FCSTD DOCUMENT  (FreeCAD 1.0R39319 (Git))
Label: plug-mount
License: All rights reserved
LicenseURL: https://en.wikipedia.org/wiki/All_rights_reserved
objects: Sketcher::SketchObject×2, PartDesign::Body×2
note: 6 computed .brp shape members not serialized (recipe doc carries the construction recipe); baked Part::Feature solids carry a one-line shape summary decoded from their .brp

FEATURE [Sketcher::SketchObject] Sketch  label="acrylic"
  ArcFitTolerance = 1e-06
  AttachmentSupport = -> [XY_Plane]
  FullyConstrained = true
  MakeInternals = false
  MapMode = 5
  sketch-geometry (84):
    g0: LineSegment StartX=0 StartY=9.525 StartZ=0 EndX=0 EndY=-9.525 EndZ=0
    g1: LineSegment StartX=0 StartY=-9.525 StartZ=0 EndX=12 EndY=-9.525 EndZ=0
    g2: LineSegment StartX=12 StartY=9.525 StartZ=0 EndX=0 EndY=9.525 EndZ=0
    g3: Circle CenterX=6 CenterY=12.7 CenterZ=0 NormalX=0 NormalY=0 NormalZ=1 AngleXU=0 Radius=1.5
    g4: Circle CenterX=6 CenterY=-12.7 CenterZ=0 NormalX=0 NormalY=0 NormalZ=1 AngleXU=0 Radius=1.5
    g5: LineSegment [constr] StartX=6 StartY=12.7 StartZ=0 EndX=6 EndY=-12.7 EndZ=0
    g6: LineSegment StartX=12 StartY=9.525 StartZ=0 EndX=12 EndY=-9.525 EndZ=0
    g7: GeomPoint X=6 Y=0 Z=0
    g8: LineSegment [constr] StartX=-2 StartY=17.5 StartZ=0 EndX=-2 EndY=-17.5 EndZ=0
    g9: LineSegment [constr] StartX=-2 StartY=-17.5 StartZ=0 EndX=14 EndY=-17.5 EndZ=0
    g10: LineSegment [constr] StartX=14 StartY=-17.5 StartZ=0 EndX=14 EndY=17.5 EndZ=0
    g11: LineSegment [constr] StartX=14 StartY=17.5 StartZ=0 EndX=-2 EndY=17.5 EndZ=0
    g12: LineSegment StartX=16 StartY=9.525 StartZ=0 EndX=16 EndY=-9.525 EndZ=0
    g13: LineSegment StartX=16 StartY=-9.525 StartZ=0 EndX=28 EndY=-9.525 EndZ=0
    g14: LineSegment StartX=28 StartY=9.525 StartZ=0 EndX=16 EndY=9.525 EndZ=0
    g15: Circle CenterX=22 CenterY=12.7 CenterZ=0 NormalX=0 NormalY=0 NormalZ=1 AngleXU=0 Radius=1.5
    g16: Circle CenterX=22 CenterY=-12.7 CenterZ=0 NormalX=0 NormalY=0 NormalZ=1 AngleXU=0 Radius=1.5
    g17: LineSegment [constr] StartX=22 StartY=12.7 StartZ=0 EndX=22 EndY=-12.7 EndZ=0
    g18: LineSegment StartX=28 StartY=9.525 StartZ=0 EndX=28 EndY=-9.525 EndZ=0
    g19: GeomPoint X=22 Y=5e-16 Z=0
    g20: LineSegment [constr] StartX=14 StartY=17.5 StartZ=0 EndX=14 EndY=-17.5 EndZ=0
    g21: LineSegment [constr] StartX=14 StartY=-17.5 StartZ=0 EndX=30 EndY=-17.5 EndZ=0
    g22: LineSegment [constr] StartX=30 StartY=-17.5 StartZ=0 EndX=30 EndY=17.5 EndZ=0
    g23: LineSegment [constr] StartX=30 StartY=17.5 StartZ=0 EndX=14 EndY=17.5 EndZ=0
    g24: LineSegment StartX=32 StartY=9.525 StartZ=0 EndX=32 EndY=-9.525 EndZ=0
    g25: LineSegment StartX=32 StartY=-9.525 StartZ=0 EndX=44 EndY=-9.525 EndZ=0
    g26: LineSegment StartX=44 StartY=9.525 StartZ=0 EndX=32 EndY=9.525 EndZ=0
    g27: Circle CenterX=38 CenterY=12.7 CenterZ=0 NormalX=0 NormalY=0 NormalZ=1 AngleXU=0 Radius=1.5
    g28: Circle CenterX=38 CenterY=-12.7 CenterZ=0 NormalX=0 NormalY=0 NormalZ=1 AngleXU=0 Radius=1.5
    g29: LineSegment [constr] StartX=38 StartY=12.7 StartZ=0 EndX=38 EndY=-12.7 EndZ=0
    g30: LineSegment StartX=44 StartY=9.525 StartZ=0 EndX=44 EndY=-9.525 EndZ=0
    g31: GeomPoint X=38 Y=-7e-16 Z=0
    g32: LineSegment [constr] StartX=30 StartY=17.5 StartZ=0 EndX=30 EndY=-17.5 EndZ=0
    g33: LineSegment [constr] StartX=30 StartY=-17.5 StartZ=0 EndX=46 EndY=-17.5 EndZ=0
    g34: LineSegment [constr] StartX=46 StartY=-17.5 StartZ=0 EndX=46 EndY=17.5 EndZ=0
    g35: LineSegment [constr] StartX=46 StartY=17.5 StartZ=0 EndX=30 EndY=17.5 EndZ=0
    g36: LineSegment StartX=48 StartY=9.525 StartZ=0 EndX=48 EndY=-9.525 EndZ=0
    g37: LineSegment StartX=48 StartY=-9.525 StartZ=0 EndX=60 EndY=-9.525 EndZ=0
    g38: LineSegment StartX=60 StartY=9.525 StartZ=0 EndX=48 EndY=9.525 EndZ=0
    g39: Circle CenterX=54 CenterY=12.7 CenterZ=0 NormalX=0 NormalY=0 NormalZ=1 AngleXU=0 Radius=1.5
    g40: Circle CenterX=54 CenterY=-12.7 CenterZ=0 NormalX=0 NormalY=0 NormalZ=1 AngleXU=0 Radius=1.5
    g41: LineSegment [constr] StartX=54 StartY=12.7 StartZ=0 EndX=54 EndY=-12.7 EndZ=0
    g42: LineSegment StartX=60 StartY=9.525 StartZ=0 EndX=60 EndY=-9.525 EndZ=0
    g43: GeomPoint X=54 Y=-6e-16 Z=0
    g44: LineSegment [constr] StartX=46 StartY=17.5 StartZ=0 EndX=46 EndY=-17.5 EndZ=0
    g45: LineSegment [constr] StartX=46 StartY=-17.5 StartZ=0 EndX=62 EndY=-17.5 EndZ=0
    g46: LineSegment [constr] StartX=62 StartY=-17.5 StartZ=0 EndX=62 EndY=17.5 EndZ=0
    g47: LineSegment [constr] StartX=62 StartY=17.5 StartZ=0 EndX=46 EndY=17.5 EndZ=0
    g48: LineSegment StartX=64 StartY=9.525 StartZ=0 EndX=64 EndY=-9.525 EndZ=0
    g49: LineSegment StartX=64 StartY=-9.525 StartZ=0 EndX=76 EndY=-9.525 EndZ=0
    g50: LineSegment StartX=76 StartY=9.525 StartZ=0 EndX=64 EndY=9.525 EndZ=0
    g51: Circle CenterX=70 CenterY=12.7 CenterZ=0 NormalX=0 NormalY=0 NormalZ=1 AngleXU=0 Radius=1.5
    g52: Circle CenterX=70 CenterY=-12.7 CenterZ=0 NormalX=0 NormalY=0 NormalZ=1 AngleXU=0 Radius=1.5
    g53: LineSegment [constr] StartX=70 StartY=12.7 StartZ=0 EndX=70 EndY=-12.7 EndZ=0
    g54: LineSegment StartX=76 StartY=9.525 StartZ=0 EndX=76 EndY=-9.525 EndZ=0
    g55: GeomPoint X=70 Y=-1.1e-15 Z=0
    g56: LineSegment [constr] StartX=62 StartY=17.5 StartZ=0 EndX=62 EndY=-17.5 EndZ=0
    g57: LineSegment [constr] StartX=62 StartY=-17.5 StartZ=0 EndX=78 EndY=-17.5 EndZ=0
    g58: LineSegment [constr] StartX=78 StartY=-17.5 StartZ=0 EndX=78 EndY=17.5 EndZ=0
    g59: LineSegment [constr] StartX=78 StartY=17.5 StartZ=0 EndX=62 EndY=17.5 EndZ=0
    g60: LineSegment StartX=80 StartY=9.525 StartZ=0 EndX=80 EndY=-9.525 EndZ=0
    g61: LineSegment StartX=80 StartY=-9.525 StartZ=0 EndX=92 EndY=-9.525 EndZ=0
    g62: LineSegment StartX=92 StartY=9.525 StartZ=0 EndX=80 EndY=9.525 EndZ=0
    g63: Circle CenterX=86 CenterY=12.7 CenterZ=0 NormalX=0 NormalY=0 NormalZ=1 AngleXU=0 Radius=1.5
    g64: Circle CenterX=86 CenterY=-12.7 CenterZ=0 NormalX=0 NormalY=0 NormalZ=1 AngleXU=0 Radius=1.5
    g65: LineSegment [constr] StartX=86 StartY=12.7 StartZ=0 EndX=86 EndY=-12.7 EndZ=0
    g66: LineSegment StartX=92 StartY=9.525 StartZ=0 EndX=92 EndY=-9.525 EndZ=0
    g67: GeomPoint X=86 Y=5.1e-15 Z=0
    g68: LineSegment [constr] StartX=78 StartY=17.5 StartZ=0 EndX=78 EndY=-17.5 EndZ=0
    g69: LineSegment [constr] StartX=78 StartY=-17.5 StartZ=0 EndX=94 EndY=-17.5 EndZ=0
    g70: LineSegment [constr] StartX=94 StartY=-17.5 StartZ=0 EndX=94 EndY=17.5 EndZ=0
    g71: LineSegment [constr] StartX=94 StartY=17.5 StartZ=0 EndX=78 EndY=17.5 EndZ=0
    g72: LineSegment StartX=-12 StartY=27.5 StartZ=0 EndX=-12 EndY=-27.5 EndZ=0
    g73: LineSegment StartX=-12 StartY=-27.5 StartZ=0 EndX=104 EndY=-27.5 EndZ=0
    g74: LineSegment StartX=104 StartY=-27.5 StartZ=0 EndX=104 EndY=27.5 EndZ=0
    g75: LineSegment StartX=104 StartY=27.5 StartZ=0 EndX=-12 EndY=27.5 EndZ=0
    g76: LineSegment [constr] StartX=-2 StartY=17.5 StartZ=0 EndX=-12 EndY=17.5 EndZ=0
    g77: LineSegment [constr] StartX=94 StartY=17.5 StartZ=0 EndX=104 EndY=17.5 EndZ=0
    g78: LineSegment [constr] StartX=-2 StartY=-17.5 StartZ=0 EndX=-2 EndY=-27.5 EndZ=0
    g79: LineSegment [constr] StartX=-2 StartY=17.5 StartZ=0 EndX=-2 EndY=27.5 EndZ=0
    g80: Circle CenterX=-7.2375 CenterY=22.7375 CenterZ=0 NormalX=0 NormalY=0 NormalZ=1 AngleXU=0 Radius=1.7526
    g81: Circle CenterX=-7.2375 CenterY=-22.7375 CenterZ=0 NormalX=0 NormalY=0 NormalZ=1 AngleXU=0 Radius=1.7526
    g82: Circle CenterX=99.2375 CenterY=-22.7375 CenterZ=0 NormalX=0 NormalY=0 NormalZ=1 AngleXU=0 Radius=1.7526
    g83: Circle CenterX=99.2375 CenterY=22.7375 CenterZ=0 NormalX=0 NormalY=0 NormalZ=1 AngleXU=0 Radius=1.7526
  constraints (221):
    c: Coincident(g0,g1)
    c: Vertical(g0)
    c: Horizontal(g2)
    c: Equal(g4,g3)
    c: Symmetric(g3,g4,g-1)
    c: DistanceY(g4,g3) = 25.4
    c: Coincident(g5,g3)
    c: Coincident(g5,g4)
    c: Symmetric(g1,g0,g5)
    c: Diameter(g4) = 3
    c: Coincident(g6,g2)
    c: Coincident(g6,g1)
    c: DistanceY(g6,g6) = 19.05
    c: PointOnObject(g7,g-1)
    c: PointOnObject(g7,g5)
    c: Coincident(g2,g0)
    c: Symmetric(g2,g1,g-1)
    c: DistanceX(g2,g2) = 12
    c: PointOnObject(g0,g-2)
    c: Coincident(g8,g9)
    c: Coincident(g9,g10)
    c: Coincident(g10,g11)
    c: Coincident(g11,g8)
    c: Vertical(g8)
    c: Vertical(g10)
    c: Horizontal(g9)
    c: Horizontal(g11)
    c: DistanceX(g11,g11) = 16
    c: DistanceY(g10,g10) = 35
    c: Symmetric(g8,g10,g7)
    c: Coincident(g12,g13)
    c: Coincident(g24,g25)
    c: Coincident(g36,g37)
    c: Coincident(g48,g49)
    c: Coincident(g60,g61)
    c: Vertical(g12)
    c: Vertical(g24)
    c: Vertical(g36)
    c: Vertical(g48)
    c: Vertical(g60)
    c: Horizontal(g14)
    c: Horizontal(g26)
    c: Horizontal(g38)
    c: Horizontal(g50)
    c: Horizontal(g62)
    c: Equal(g16,g15)
    c: Equal(g28,g27)
    c: Equal(g40,g39)
    c: Equal(g52,g51)
    c: Equal(g64,g63)
    c: DistanceY(g16,g15) = 25.4
    c: DistanceY(g28,g27) = 25.4
    c: DistanceY(g40,g39) = 25.4
    c: DistanceY(g52,g51) = 25.4
    c: DistanceY(g64,g63) = 25.4
    c: Coincident(g17,g15)
    c: Coincident(g29,g27)
    c: Coincident(g41,g39)
    c: Coincident(g53,g51)
    c: Coincident(g65,g63)
    c: Coincident(g17,g16)
    c: Coincident(g29,g28)
    c: Coincident(g41,g40)
    c: Coincident(g53,g52)
    c: Coincident(g65,g64)
    c: Symmetric(g13,g12,g17)
    c: Symmetric(g25,g24,g29)
    c: Symmetric(g37,g36,g41)
    c: Symmetric(g49,g48,g53)
    c: Symmetric(g61,g60,g65)
    c: Diameter(g16) = 3
    c: Diameter(g28) = 3
    c: Diameter(g40) = 3
    c: Diameter(g52) = 3
    c: Diameter(g64) = 3
    c: Coincident(g18,g14)
    c: Coincident(g30,g26)
    c: Coincident(g42,g38)
    c: Coincident(g54,g50)
    c: Coincident(g66,g62)
    c: Coincident(g18,g13)
    c: Coincident(g30,g25)
    c: Coincident(g42,g37)
    c: Coincident(g54,g49)
    c: Coincident(g66,g61)
    c: DistanceY(g18,g18) = 19.05
    c: DistanceY(g30,g30) = 19.05
    c: DistanceY(g42,g42) = 19.05
    c: DistanceY(g54,g54) = 19.05
    c: DistanceY(g66,g66) = 19.05
    c: PointOnObject(g19,g17)
    c: PointOnObject(g31,g29)
    c: PointOnObject(g43,g41)
    c: PointOnObject(g55,g53)
    c: PointOnObject(g67,g65)
    c: Coincident(g14,g12)
    c: Coincident(g26,g24)
    c: Coincident(g38,g36)
    c: Coincident(g50,g48)
    c: Coincident(g62,g60)
    c: DistanceX(g14,g14) = 12
    c: DistanceX(g26,g26) = 12
    c: DistanceX(g38,g38) = 12
    c: DistanceX(g50,g50) = 12
    c: DistanceX(g62,g62) = 12
    c: Coincident(g20,g21)
    c: Coincident(g32,g33)
    c: Coincident(g44,g45)
    c: Coincident(g56,g57)
    c: Coincident(g68,g69)
    c: Coincident(g21,g22)
    c: Coincident(g33,g34)
    c: Coincident(g45,g46)
    c: Coincident(g57,g58)
    c: Coincident(g69,g70)
    c: Coincident(g22,g23)
    c: Coincident(g34,g35)
    c: Coincident(g46,g47)
    c: Coincident(g58,g59)
    c: Coincident(g70,g71)
    c: Coincident(g23,g20)
    c: Coincident(g35,g32)
    c: Coincident(g47,g44)
    c: Coincident(g59,g56)
    c: Coincident(g71,g68)
    c: Vertical(g20)
    c: Vertical(g32)
    c: Vertical(g44)
    c: Vertical(g56)
    c: Vertical(g68)
    c: Vertical(g22)
    c: Vertical(g34)
    c: Vertical(g46)
    c: Vertical(g58)
    c: Vertical(g70)
    c: Horizontal(g21)
    c: Horizontal(g33)
    c: Horizontal(g45)
    c: Horizontal(g57)
    c: Horizontal(g69)
    c: Horizontal(g23)
    c: Horizontal(g35)
    c: Horizontal(g47)
    c: Horizontal(g59)
    c: Horizontal(g71)
    c: DistanceX(g23,g23) = 16
    c: DistanceX(g35,g35) = 16
    c: DistanceX(g47,g47) = 16
    c: DistanceX(g59,g59) = 16
    c: DistanceX(g71,g71) = 16
    c: DistanceY(g22,g22) = 35
    c: DistanceY(g34,g34) = 35
    c: DistanceY(g46,g46) = 35
    c: DistanceY(g58,g58) = 35
    c: DistanceY(g70,g70) = 35
    c: Symmetric(g20,g22,g19)
    c: Symmetric(g32,g34,g31)
    c: Symmetric(g44,g46,g43)
    c: Symmetric(g56,g58,g55)
    c: Symmetric(g68,g70,g67)
    c: Coincident(g72,g73)
    c: Coincident(g73,g74)
    c: Coincident(g74,g75)
    c: Coincident(g75,g72)
    c: Vertical(g72)
    c: Vertical(g74)
    c: Horizontal(g73)
    c: Horizontal(g75)
    c: Coincident(g76,g8)
    c: PointOnObject(g76,g72)
    c: Horizontal(g76)
    c: Coincident(g77,g70)
    c: PointOnObject(g77,g74)
    c: Horizontal(g77)
    c: Equal(g76,g77)
    c: DistanceX(g76,g76) = 10
    c: Vertical(g65)
    c: Vertical(g66)
    c: Coincident(g10,g20)
    c: Coincident(g22,g32)
    c: Coincident(g34,g44)
    c: Coincident(g46,g56)
    c: Coincident(g58,g68)
    c: Coincident(g78,g8)
    c: Vertical(g78)
    c: Coincident(g79,g8)
    c: PointOnObject(g79,g75)
    c: Vertical(g79)
    c: Equal(g79,g78)
    c: PointOnObject(g78,g73)
    c: DistanceY(g78,g78) = 10
    c: Horizontal(g13)
    c: Horizontal(g25)
    c: Horizontal(g37)
    c: Horizontal(g49)
    c: Vertical(g18)
    c: Vertical(g30)
    c: Vertical(g42)
    c: Vertical(g54)
    c: Horizontal(g60,g48)
    c: Horizontal(g36,g48)
    c: Horizontal(g36,g24)
    c: Horizontal(g24,g12)
    c: Horizontal(g1,g12)
    c: Horizontal(g3,g15)
    c: Horizontal(g15,g27)
    c: Horizontal(g27,g39)
    c: Horizontal(g39,g51)
    c: Horizontal(g51,g63)
    c: Vertical(g83,g82)
    c: Vertical(g81,g80)
    c: Horizontal(g83,g80)
    c: DistanceY(g80,g72) = 4.7625
    c: DistanceX(g72,g80) = 4.7625
    c: Equal(g80,g81)
    c: Equal(g81,g82)
    c: Equal(g82,g83)
    c: Diameter(g81) = 3.5052
    c: DistanceX(g82,g73) = 4.7625
    c: DistanceY(g72,g81) = 4.7625
    c: Horizontal(g82,g81)
FEATURE [PartDesign::Body] Body
  AllowCompound = false
  Group = -> [Sketch]
  Origin = -> Origin
FEATURE [Sketcher::SketchObject] Sketch001  label="wood"
  ArcFitTolerance = 1e-06
  AttachmentSupport = -> [XY_Plane001]
  FullyConstrained = true
  MakeInternals = false
  MapMode = 5
  sketch-geometry (84):
    g0: LineSegment StartX=0 StartY=9.525 StartZ=0 EndX=0 EndY=-9.525 EndZ=0
    g1: LineSegment StartX=0 StartY=-9.525 StartZ=0 EndX=12 EndY=-9.525 EndZ=0
    g2: LineSegment StartX=12 StartY=9.525 StartZ=0 EndX=0 EndY=9.525 EndZ=0
    g3: Circle CenterX=6 CenterY=12.7 CenterZ=0 NormalX=0 NormalY=0 NormalZ=1 AngleXU=0 Radius=3.175
    g4: Circle CenterX=6 CenterY=-12.7 CenterZ=0 NormalX=0 NormalY=0 NormalZ=1 AngleXU=0 Radius=3.175
    g5: LineSegment [constr] StartX=6 StartY=12.7 StartZ=0 EndX=6 EndY=-12.7 EndZ=0
    g6: LineSegment StartX=12 StartY=9.525 StartZ=0 EndX=12 EndY=-9.525 EndZ=0
    g7: GeomPoint X=6 Y=0 Z=0
    g8: LineSegment [constr] StartX=-2 StartY=17.5 StartZ=0 EndX=-2 EndY=-17.5 EndZ=0
    g9: LineSegment [constr] StartX=-2 StartY=-17.5 StartZ=0 EndX=14 EndY=-17.5 EndZ=0
    g10: LineSegment [constr] StartX=14 StartY=-17.5 StartZ=0 EndX=14 EndY=17.5 EndZ=0
    g11: LineSegment [constr] StartX=14 StartY=17.5 StartZ=0 EndX=-2 EndY=17.5 EndZ=0
    g12: LineSegment StartX=16 StartY=9.525 StartZ=0 EndX=16 EndY=-9.525 EndZ=0
    g13: LineSegment StartX=16 StartY=-9.525 StartZ=0 EndX=28 EndY=-9.525 EndZ=0
    g14: LineSegment StartX=28 StartY=9.525 StartZ=0 EndX=16 EndY=9.525 EndZ=0
    g15: Circle CenterX=22 CenterY=12.7 CenterZ=0 NormalX=0 NormalY=0 NormalZ=1 AngleXU=0 Radius=3.175
    g16: Circle CenterX=22 CenterY=-12.7 CenterZ=0 NormalX=0 NormalY=0 NormalZ=1 AngleXU=0 Radius=3.175
    g17: LineSegment [constr] StartX=22 StartY=12.7 StartZ=0 EndX=22 EndY=-12.7 EndZ=0
    g18: LineSegment StartX=28 StartY=9.525 StartZ=0 EndX=28 EndY=-9.525 EndZ=0
    g19: GeomPoint X=22 Y=-4e-16 Z=0
    g20: LineSegment [constr] StartX=14 StartY=17.5 StartZ=0 EndX=14 EndY=-17.5 EndZ=0
    g21: LineSegment [constr] StartX=14 StartY=-17.5 StartZ=0 EndX=30 EndY=-17.5 EndZ=0
    g22: LineSegment [constr] StartX=30 StartY=-17.5 StartZ=0 EndX=30 EndY=17.5 EndZ=0
    g23: LineSegment [constr] StartX=30 StartY=17.5 StartZ=0 EndX=14 EndY=17.5 EndZ=0
    g24: LineSegment StartX=32 StartY=9.525 StartZ=0 EndX=32 EndY=-9.525 EndZ=0
    g25: LineSegment StartX=32 StartY=-9.525 StartZ=0 EndX=44 EndY=-9.525 EndZ=0
    g26: LineSegment StartX=44 StartY=9.525 StartZ=0 EndX=32 EndY=9.525 EndZ=0
    g27: Circle CenterX=38 CenterY=12.7 CenterZ=0 NormalX=0 NormalY=0 NormalZ=1 AngleXU=0 Radius=3.175
    g28: Circle CenterX=38 CenterY=-12.7 CenterZ=0 NormalX=0 NormalY=0 NormalZ=1 AngleXU=0 Radius=3.175
    g29: LineSegment [constr] StartX=38 StartY=12.7 StartZ=0 EndX=38 EndY=-12.7 EndZ=0
    g30: LineSegment StartX=44 StartY=9.525 StartZ=0 EndX=44 EndY=-9.525 EndZ=0
    g31: GeomPoint X=38 Y=-4e-16 Z=0
    g32: LineSegment [constr] StartX=30 StartY=17.5 StartZ=0 EndX=30 EndY=-17.5 EndZ=0
    g33: LineSegment [constr] StartX=30 StartY=-17.5 StartZ=0 EndX=46 EndY=-17.5 EndZ=0
    g34: LineSegment [constr] StartX=46 StartY=-17.5 StartZ=0 EndX=46 EndY=17.5 EndZ=0
    g35: LineSegment [constr] StartX=46 StartY=17.5 StartZ=0 EndX=30 EndY=17.5 EndZ=0
    g36: LineSegment StartX=48 StartY=9.525 StartZ=0 EndX=48 EndY=-9.525 EndZ=0
    g37: LineSegment StartX=48 StartY=-9.525 StartZ=0 EndX=60 EndY=-9.525 EndZ=0
    g38: LineSegment StartX=60 StartY=9.525 StartZ=0 EndX=48 EndY=9.525 EndZ=0
    g39: Circle CenterX=54 CenterY=12.7 CenterZ=0 NormalX=0 NormalY=0 NormalZ=1 AngleXU=0 Radius=3.175
    g40: Circle CenterX=54 CenterY=-12.7 CenterZ=0 NormalX=0 NormalY=0 NormalZ=1 AngleXU=0 Radius=3.175
    g41: LineSegment [constr] StartX=54 StartY=12.7 StartZ=0 EndX=54 EndY=-12.7 EndZ=0
    g42: LineSegment StartX=60 StartY=9.525 StartZ=0 EndX=60 EndY=-9.525 EndZ=0
    g43: GeomPoint X=54 Y=-3e-16 Z=0
    g44: LineSegment [constr] StartX=46 StartY=17.5 StartZ=0 EndX=46 EndY=-17.5 EndZ=0
    g45: LineSegment [constr] StartX=46 StartY=-17.5 StartZ=0 EndX=62 EndY=-17.5 EndZ=0
    g46: LineSegment [constr] StartX=62 StartY=-17.5 StartZ=0 EndX=62 EndY=17.5 EndZ=0
    g47: LineSegment [constr] StartX=62 StartY=17.5 StartZ=0 EndX=46 EndY=17.5 EndZ=0
    g48: LineSegment StartX=64 StartY=9.525 StartZ=0 EndX=64 EndY=-9.525 EndZ=0
    g49: LineSegment StartX=64 StartY=-9.525 StartZ=0 EndX=76 EndY=-9.525 EndZ=0
    g50: LineSegment StartX=76 StartY=9.525 StartZ=0 EndX=64 EndY=9.525 EndZ=0
    g51: Circle CenterX=70 CenterY=12.7 CenterZ=0 NormalX=0 NormalY=0 NormalZ=1 AngleXU=0 Radius=3.175
    g52: Circle CenterX=70 CenterY=-12.7 CenterZ=0 NormalX=0 NormalY=0 NormalZ=1 AngleXU=0 Radius=3.175
    g53: LineSegment [constr] StartX=70 StartY=12.7 StartZ=0 EndX=70 EndY=-12.7 EndZ=0
    g54: LineSegment StartX=76 StartY=9.525 StartZ=0 EndX=76 EndY=-9.525 EndZ=0
    g55: GeomPoint X=70 Y=-8e-16 Z=0
    g56: LineSegment [constr] StartX=62 StartY=17.5 StartZ=0 EndX=62 EndY=-17.5 EndZ=0
    g57: LineSegment [constr] StartX=62 StartY=-17.5 StartZ=0 EndX=78 EndY=-17.5 EndZ=0
    g58: LineSegment [constr] StartX=78 StartY=-17.5 StartZ=0 EndX=78 EndY=17.5 EndZ=0
    g59: LineSegment [constr] StartX=78 StartY=17.5 StartZ=0 EndX=62 EndY=17.5 EndZ=0
    g60: LineSegment StartX=80 StartY=9.525 StartZ=0 EndX=80 EndY=-9.525 EndZ=0
    g61: LineSegment StartX=80 StartY=-9.525 StartZ=0 EndX=92 EndY=-9.525 EndZ=0
    g62: LineSegment StartX=92 StartY=9.525 StartZ=0 EndX=80 EndY=9.525 EndZ=0
    g63: Circle CenterX=86 CenterY=12.7 CenterZ=0 NormalX=0 NormalY=0 NormalZ=1 AngleXU=0 Radius=3.175
    g64: Circle CenterX=86 CenterY=-12.7 CenterZ=0 NormalX=0 NormalY=0 NormalZ=1 AngleXU=0 Radius=3.175
    g65: LineSegment [constr] StartX=86 StartY=12.7 StartZ=0 EndX=86 EndY=-12.7 EndZ=0
    g66: LineSegment StartX=92 StartY=9.525 StartZ=0 EndX=92 EndY=-9.525 EndZ=0
    g67: GeomPoint X=86 Y=6e-16 Z=0
    g68: LineSegment [constr] StartX=78 StartY=17.5 StartZ=0 EndX=78 EndY=-17.5 EndZ=0
    g69: LineSegment [constr] StartX=78 StartY=-17.5 StartZ=0 EndX=94 EndY=-17.5 EndZ=0
    g70: LineSegment [constr] StartX=94 StartY=-17.5 StartZ=0 EndX=94 EndY=17.5 EndZ=0
    g71: LineSegment [constr] StartX=94 StartY=17.5 StartZ=0 EndX=78 EndY=17.5 EndZ=0
    g72: LineSegment StartX=-12 StartY=27.5 StartZ=0 EndX=-12 EndY=-27.5 EndZ=0
    g73: LineSegment StartX=-12 StartY=-27.5 StartZ=0 EndX=104 EndY=-27.5 EndZ=0
    g74: LineSegment StartX=104 StartY=-27.5 StartZ=0 EndX=104 EndY=27.5 EndZ=0
    g75: LineSegment StartX=104 StartY=27.5 StartZ=0 EndX=-12 EndY=27.5 EndZ=0
    g76: LineSegment [constr] StartX=-2 StartY=17.5 StartZ=0 EndX=-12 EndY=17.5 EndZ=0
    g77: LineSegment [constr] StartX=94 StartY=17.5 StartZ=0 EndX=104 EndY=17.5 EndZ=0
    g78: LineSegment [constr] StartX=-2 StartY=-17.5 StartZ=0 EndX=-2 EndY=-27.5 EndZ=0
    g79: LineSegment [constr] StartX=-2 StartY=17.5 StartZ=0 EndX=-2 EndY=27.5 EndZ=0
    g80: Circle CenterX=-7.2375 CenterY=22.7375 CenterZ=0 NormalX=0 NormalY=0 NormalZ=1 AngleXU=0 Radius=0.992188
    g81: Circle CenterX=-7.2375 CenterY=-22.7375 CenterZ=0 NormalX=0 NormalY=0 NormalZ=1 AngleXU=0 Radius=0.992188
    g82: Circle CenterX=99.2375 CenterY=-22.7375 CenterZ=0 NormalX=0 NormalY=0 NormalZ=1 AngleXU=0 Radius=0.992188
    g83: Circle CenterX=99.2375 CenterY=22.7375 CenterZ=0 NormalX=0 NormalY=0 NormalZ=1 AngleXU=0 Radius=0.992188
  constraints (221):
    c: Coincident(g0,g1)
    c: Vertical(g0)
    c: Horizontal(g2)
    c: Symmetric(g3,g4,g-1)
    c: DistanceY(g4,g3) = 25.4
    c: Coincident(g5,g3)
    c: Coincident(g5,g4)
    c: Symmetric(g1,g0,g5)
    c: Coincident(g6,g2)
    c: Coincident(g6,g1)
    c: DistanceY(g6,g6) = 19.05
    c: PointOnObject(g7,g-1)
    c: PointOnObject(g7,g5)
    c: Coincident(g2,g0)
    c: Symmetric(g2,g1,g-1)
    c: DistanceX(g2,g2) = 12
    c: PointOnObject(g0,g-2)
    c: Coincident(g8,g9)
    c: Coincident(g9,g10)
    c: Coincident(g10,g11)
    c: Coincident(g11,g8)
    c: Vertical(g8)
    c: Vertical(g10)
    c: Horizontal(g9)
    c: Horizontal(g11)
    c: DistanceX(g11,g11) = 16
    c: DistanceY(g10,g10) = 35
    c: Symmetric(g8,g10,g7)
    c: Coincident(g12,g13)
    c: Coincident(g24,g25)
    c: Coincident(g36,g37)
    c: Coincident(g48,g49)
    c: Coincident(g60,g61)
    c: Vertical(g12)
    c: Vertical(g24)
    c: Vertical(g36)
    c: Vertical(g48)
    c: Vertical(g60)
    c: Horizontal(g14)
    c: Horizontal(g26)
    c: Horizontal(g38)
    c: Horizontal(g50)
    c: Horizontal(g62)
    c: Equal(g64,g63)
    c: DistanceY(g16,g15) = 25.4
    c: DistanceY(g28,g27) = 25.4
    c: DistanceY(g40,g39) = 25.4
    c: DistanceY(g52,g51) = 25.4
    c: DistanceY(g64,g63) = 25.4
    c: Coincident(g17,g15)
    c: Coincident(g29,g27)
    c: Coincident(g41,g39)
    c: Coincident(g53,g51)
    c: Coincident(g65,g63)
    c: Coincident(g17,g16)
    c: Coincident(g29,g28)
    c: Coincident(g41,g40)
    c: Coincident(g53,g52)
    c: Coincident(g65,g64)
    c: Symmetric(g13,g12,g17)
    c: Symmetric(g25,g24,g29)
    c: Symmetric(g37,g36,g41)
    c: Symmetric(g49,g48,g53)
    c: Symmetric(g61,g60,g65)
    c: Coincident(g18,g14)
    c: Coincident(g30,g26)
    c: Coincident(g42,g38)
    c: Coincident(g54,g50)
    c: Coincident(g66,g62)
    c: Coincident(g18,g13)
    c: Coincident(g30,g25)
    c: Coincident(g42,g37)
    c: Coincident(g54,g49)
    c: Coincident(g66,g61)
    c: DistanceY(g18,g18) = 19.05
    c: DistanceY(g30,g30) = 19.05
    c: DistanceY(g42,g42) = 19.05
    c: DistanceY(g54,g54) = 19.05
    c: DistanceY(g66,g66) = 19.05
    c: PointOnObject(g19,g17)
    c: PointOnObject(g31,g29)
    c: PointOnObject(g43,g41)
    c: PointOnObject(g55,g53)
    c: PointOnObject(g67,g65)
    c: Coincident(g14,g12)
    c: Coincident(g26,g24)
    c: Coincident(g38,g36)
    c: Coincident(g50,g48)
    c: Coincident(g62,g60)
    c: DistanceX(g14,g14) = 12
    c: DistanceX(g26,g26) = 12
    c: DistanceX(g38,g38) = 12
    c: DistanceX(g50,g50) = 12
    c: DistanceX(g62,g62) = 12
    c: Coincident(g20,g21)
    c: Coincident(g32,g33)
    c: Coincident(g44,g45)
    c: Coincident(g56,g57)
    c: Coincident(g68,g69)
    c: Coincident(g21,g22)
    c: Coincident(g33,g34)
    c: Coincident(g45,g46)
    c: Coincident(g57,g58)
    c: Coincident(g69,g70)
    c: Coincident(g22,g23)
    c: Coincident(g34,g35)
    c: Coincident(g46,g47)
    c: Coincident(g58,g59)
    c: Coincident(g70,g71)
    c: Coincident(g23,g20)
    c: Coincident(g35,g32)
    c: Coincident(g47,g44)
    c: Coincident(g59,g56)
    c: Coincident(g71,g68)
    c: Vertical(g20)
    c: Vertical(g32)
    c: Vertical(g44)
    c: Vertical(g56)
    c: Vertical(g68)
    c: Vertical(g22)
    c: Vertical(g34)
    c: Vertical(g46)
    c: Vertical(g58)
    c: Vertical(g70)
    c: Horizontal(g21)
    c: Horizontal(g33)
    c: Horizontal(g45)
    c: Horizontal(g57)
    c: Horizontal(g69)
    c: Horizontal(g23)
    c: Horizontal(g35)
    c: Horizontal(g47)
    c: Horizontal(g59)
    c: Horizontal(g71)
    c: DistanceX(g23,g23) = 16
    c: DistanceX(g35,g35) = 16
    c: DistanceX(g47,g47) = 16
    c: DistanceX(g59,g59) = 16
    c: DistanceX(g71,g71) = 16
    c: DistanceY(g22,g22) = 35
    c: DistanceY(g34,g34) = 35
    c: DistanceY(g46,g46) = 35
    c: DistanceY(g58,g58) = 35
    c: DistanceY(g70,g70) = 35
    c: Symmetric(g20,g22,g19)
    c: Symmetric(g32,g34,g31)
    c: Symmetric(g44,g46,g43)
    c: Symmetric(g56,g58,g55)
    c: Symmetric(g68,g70,g67)
    c: Coincident(g72,g73)
    c: Coincident(g73,g74)
    c: Coincident(g74,g75)
    c: Coincident(g75,g72)
    c: Vertical(g72)
    c: Vertical(g74)
    c: Horizontal(g73)
    c: Horizontal(g75)
    c: Coincident(g76,g8)
    c: PointOnObject(g76,g72)
    c: Horizontal(g76)
    c: Coincident(g77,g70)
    c: PointOnObject(g77,g74)
    c: Horizontal(g77)
    c: Equal(g76,g77)
    c: DistanceX(g76,g76) = 10
    c: Vertical(g65)
    c: Vertical(g66)
    c: Coincident(g10,g20)
    c: Coincident(g22,g32)
    c: Coincident(g34,g44)
    c: Coincident(g46,g56)
    c: Coincident(g58,g68)
    c: Coincident(g78,g8)
    c: Vertical(g78)
    c: Coincident(g79,g8)
    c: PointOnObject(g79,g75)
    c: Vertical(g79)
    c: Equal(g79,g78)
    c: PointOnObject(g78,g73)
    c: DistanceY(g78,g78) = 10
    c: Horizontal(g13)
    c: Horizontal(g25)
    c: Horizontal(g37)
    c: Horizontal(g49)
    c: Vertical(g18)
    c: Vertical(g30)
    c: Vertical(g42)
    c: Vertical(g54)
    c: Horizontal(g60,g48)
    c: Horizontal(g36,g48)
    c: Horizontal(g36,g24)
    c: Horizontal(g24,g12)
    c: Horizontal(g1,g12)
    c: Horizontal(g3,g15)
    c: Horizontal(g15,g27)
    c: Horizontal(g27,g39)
    c: Horizontal(g39,g51)
    c: Horizontal(g51,g63)
    c: Vertical(g83,g82)
    c: Vertical(g81,g80)
    c: Horizontal(g83,g80)
    c: DistanceY(g80,g72) = 4.7625
    c: DistanceX(g72,g80) = 4.7625
    c: Equal(g80,g81)
    c: Equal(g81,g82)
    c: Equal(g82,g83)
    c: Diameter(g81) = 1.98438
    c: DistanceX(g82,g73) = 4.7625
    c: DistanceY(g72,g81) = 4.7625
    c: Horizontal(g82,g81)
    c: Equal(g63,g51)
    c: Equal(g4,g3)
    c: Equal(g3,g15)
    c: Equal(g15,g16)
    c: Equal(g16,g28)
    c: Equal(g28,g27)
    c: Equal(g27,g39)
    c: Equal(g39,g40)
    c: Equal(g40,g52)
    c: Equal(g52,g51)
    c: Diameter(g64) = 6.35
FEATURE [PartDesign::Body] Body001
  AllowCompound = false
  Group = -> [Sketch001]
  Origin = -> Origin001
